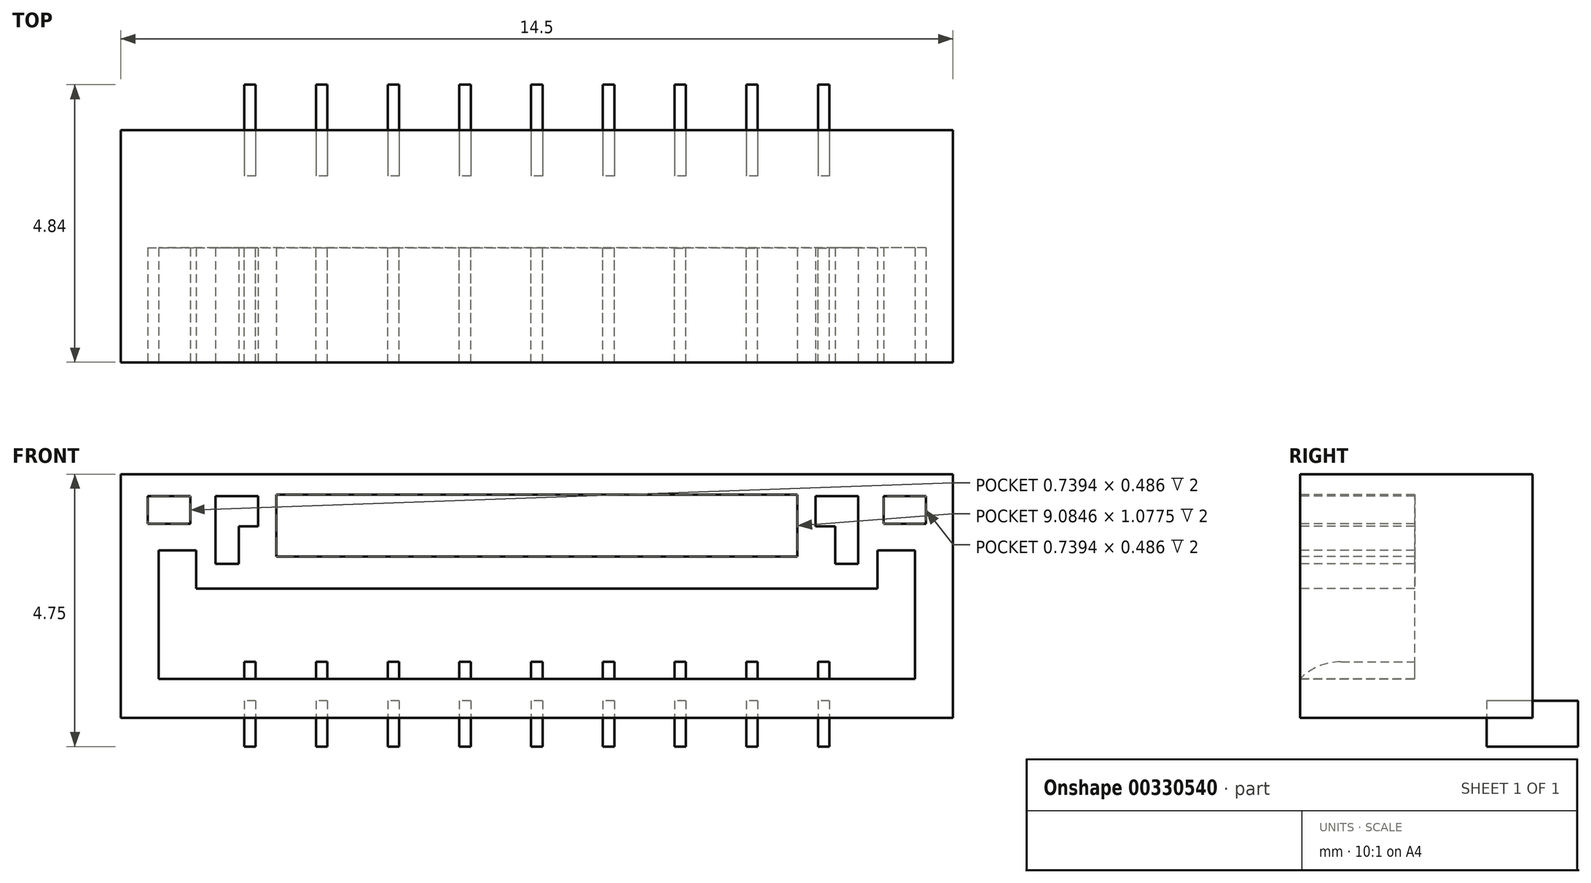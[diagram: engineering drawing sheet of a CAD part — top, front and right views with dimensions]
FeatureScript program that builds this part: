
annotation { "Feature Type Name" : "Feature", "Feature Type Description" : "" }
export const myFeature = defineFeature(function(context is Context, id is Id, definition is map)
    precondition{}
    {
        {
            var Q0;
            Q0=qCreatedBy(makeId("Top.planeOp"),FACE);
            var sketch = newSketch(context, id + "F0", { "sketchPlane" : qUnion([Q0])});
            skLineSegment(sketch, "E0.bottom", {"start": v(7.25, -2.02) * mm, "end": v(-7.25, -2.03) * mm});
            skLineSegment(sketch, "E0.top", {"start": v(7.25, 2.03) * mm, "end": v(-7.25, 2.02) * mm});
            skLineSegment(sketch, "E0.left", {"start": v(7.25, -2.02) * mm, "end": v(7.25, 2.03) * mm});
            skLineSegment(sketch, "E0.right", {"start": v(-7.25, -2.03) * mm, "end": v(-7.25, 2.02) * mm});
            skPoint(sketch, "E0.middle", {"position": v(0, 0) * mm});
            skSolve(sketch);
        }
        {
            var Q0;
            Q0 = qSketchRegion(id + "F0", true);
            extrude(context, id + "F1", {"entities" : qUnion([Q0]), "depth" : 4.25 * mm, "offsetDistance" : 25 * mm});
        }
        {
            var Q0;
            Q0=makeQuery(id+"F1.opExtrude","SWEPT_FACE",FACE,{"disambiguationData":[OSD([sQuery(id+"F0.wireOp",EDGE,"E0.bottom")])]});
            var sketch = newSketch(context, id + "F2", { "sketchPlane" : qUnion([Q0])});
            skLineSegment(sketch, "E1", {"start": v(0, 0.68) * mm, "end": v(-6.6, 0.68) * mm});
            skLineSegment(sketch, "E2", {"start": v(-6.6, 0.68) * mm, "end": v(-6.6, 2.92) * mm});
            skLineSegment(sketch, "E3", {"start": v(-6.6, 2.92) * mm, "end": v(-5.94, 2.92) * mm});
            skLineSegment(sketch, "E4", {"start": v(-5.94, 2.92) * mm, "end": v(-5.94, 2.25) * mm});
            skLineSegment(sketch, "E5", {"start": v(-5.94, 0.68) * mm, "end": v(0, 0.68) * mm});
            skLineSegment(sketch, "E6", {"start": v(0, 0.68) * mm, "end": v(0, 0.68) * mm});
            skLineSegment(sketch, "E7.bottom", {"start": v(-6.78, 3.87) * mm, "end": v(-6.04, 3.87) * mm});
            skLineSegment(sketch, "E7.top", {"start": v(-6.78, 3.38) * mm, "end": v(-6.04, 3.38) * mm});
            skLineSegment(sketch, "E7.left", {"start": v(-6.78, 3.87) * mm, "end": v(-6.78, 3.38) * mm});
            skLineSegment(sketch, "E7.right", {"start": v(-6.04, 3.87) * mm, "end": v(-6.04, 3.38) * mm});
            skLineSegment(sketch, "E8.bottom", {"start": v(-4.54, 3.89) * mm, "end": v(0, 3.89) * mm});
            skLineSegment(sketch, "E8.top", {"start": v(-4.54, 2.81) * mm, "end": v(0, 2.81) * mm});
            skLineSegment(sketch, "E8.left", {"start": v(-4.54, 3.89) * mm, "end": v(-4.54, 2.81) * mm});
            skLineSegment(sketch, "E9", {"start": v(-5.6, 3.87) * mm, "end": v(-5.6, 2.68) * mm});
            skLineSegment(sketch, "E10", {"start": v(-5.6, 2.68) * mm, "end": v(-5.2, 2.68) * mm});
            skLineSegment(sketch, "E11", {"start": v(-5.2, 2.68) * mm, "end": v(-5.2, 3.34) * mm});
            skLineSegment(sketch, "E12", {"start": v(-5.2, 3.34) * mm, "end": v(-4.86, 3.34) * mm});
            skLineSegment(sketch, "E13", {"start": v(-4.86, 3.34) * mm, "end": v(-4.86, 3.87) * mm});
            skLineSegment(sketch, "E14", {"start": v(-4.86, 3.87) * mm, "end": v(-5.6, 3.87) * mm});
            skLineSegment(sketch, "E15.MirrorCS", {"start": v(5.94, 2.92) * mm, "end": v(5.94, 2.25) * mm});
            skLineSegment(sketch, "E16.MirrorCS", {"start": v(6.78, 3.87) * mm, "end": v(6.78, 3.38) * mm});
            skLineSegment(sketch, "E17.MirrorCS", {"start": v(6.04, 3.87) * mm, "end": v(6.04, 3.38) * mm});
            skLineSegment(sketch, "E18.MirrorCS", {"start": v(5.2, 3.34) * mm, "end": v(4.86, 3.34) * mm});
            skLineSegment(sketch, "E19.MirrorCS", {"start": v(5.6, 2.68) * mm, "end": v(5.2, 2.68) * mm});
            skLineSegment(sketch, "E20.MirrorCS", {"start": v(4.86, 3.34) * mm, "end": v(4.86, 3.87) * mm});
            skLineSegment(sketch, "E21.MirrorCS", {"start": v(6.78, 3.87) * mm, "end": v(6.04, 3.87) * mm});
            skLineSegment(sketch, "E22.MirrorCS", {"start": v(6.78, 3.38) * mm, "end": v(6.04, 3.38) * mm});
            skLineSegment(sketch, "E23.MirrorCS", {"start": v(5.94, 0.68) * mm, "end": v(0, 0.68) * mm});
            skLineSegment(sketch, "E24.MirrorCS", {"start": v(6.6, 2.92) * mm, "end": v(5.94, 2.92) * mm});
            skLineSegment(sketch, "E25.MirrorCS", {"start": v(6.6, 0.68) * mm, "end": v(6.6, 2.92) * mm});
            skLineSegment(sketch, "E26.MirrorCS", {"start": v(0, 0.68) * mm, "end": v(6.6, 0.68) * mm});
            skLineSegment(sketch, "E27.MirrorCS", {"start": v(5.6, 3.87) * mm, "end": v(5.6, 2.68) * mm});
            skLineSegment(sketch, "E28.MirrorCS", {"start": v(4.54, 3.89) * mm, "end": v(4.54, 2.81) * mm});
            skLineSegment(sketch, "E29.MirrorCS", {"start": v(4.54, 3.89) * mm, "end": v(0, 3.89) * mm});
            skLineSegment(sketch, "E30.MirrorCS", {"start": v(4.54, 2.81) * mm, "end": v(0, 2.81) * mm});
            skLineSegment(sketch, "E31.MirrorCS", {"start": v(4.86, 3.87) * mm, "end": v(5.6, 3.87) * mm});
            skLineSegment(sketch, "E32.MirrorCS", {"start": v(5.2, 2.68) * mm, "end": v(5.2, 3.34) * mm});
            skLineSegment(sketch, "E33", {"start": v(-5.94, 2.25) * mm, "end": v(5.94, 2.25) * mm});
            skSolve(sketch);
        }
        {
            var Q0;
            Q0 = qSketchRegion(id + "F2", true);
            extrude(context, id + "F3", {"entities" : qUnion([Q0]), "operationType" : NewBodyOperationType.REMOVE, "oppositeDirection" : true, "depth" : 2 * mm, "offsetDistance" : 25 * mm});
        }
        {
            var Q0;
            Q0=makeQuery(id+"F3.boolean.opBoolean","COPY",FACE,{"derivedFrom":makeQuery(id+"F3.opExtrude","SWEPT_FACE",FACE,{"disambiguationData":[OSD([sQuery(id+"F2.wireOp",EDGE,"E1"),sQuery(id+"F2.wireOp",EDGE,"E5"),sQuery(id+"F2.wireOp",EDGE,"E26.MirrorCS")])]})});
            var sketch = newSketch(context, id + "F4", { "sketchPlane" : qUnion([Q0])});
            skLineSegment(sketch, "E34", {"start": v(0, -1.03) * mm, "end": v(0, -4.7) * mm, "construction": true});
            skPoint(sketch, "E34.endSnap0", {"position": v(0, -2.03) * mm});
            skLineSegment(sketch, "E35.bottom", {"start": v(-1.15, -2.03) * mm, "end": v(-1.35, -2.03) * mm});
            skLineSegment(sketch, "E35.top", {"start": v(-1.15, -0.03) * mm, "end": v(-1.35, -0.03) * mm});
            skLineSegment(sketch, "E35.left", {"start": v(-1.15, -2.03) * mm, "end": v(-1.15, -0.03) * mm});
            skLineSegment(sketch, "E35.right", {"start": v(-1.35, -2.03) * mm, "end": v(-1.35, -0.03) * mm});
            skPoint(sketch, "E35.middle", {"position": v(-1.25, -1.03) * mm});
            skPoint(sketch, "E36.1.0.0", {"position": v(-2.5, -1.03) * mm});
            skLineSegment(sketch, "E36.1.0.1", {"start": v(-2.6, -2.03) * mm, "end": v(-2.6, -0.03) * mm});
            skLineSegment(sketch, "E36.1.0.2", {"start": v(-2.4, -2.03) * mm, "end": v(-2.6, -2.03) * mm});
            skLineSegment(sketch, "E36.1.0.3", {"start": v(-2.4, -2.03) * mm, "end": v(-2.4, -0.03) * mm});
            skLineSegment(sketch, "E36.1.0.4", {"start": v(-2.4, -0.03) * mm, "end": v(-2.6, -0.03) * mm});
            skPoint(sketch, "E36.2.0.0", {"position": v(-3.75, -1.03) * mm});
            skLineSegment(sketch, "E36.2.0.1", {"start": v(-3.85, -2.03) * mm, "end": v(-3.85, -0.03) * mm});
            skLineSegment(sketch, "E36.2.0.2", {"start": v(-3.65, -2.03) * mm, "end": v(-3.85, -2.03) * mm});
            skLineSegment(sketch, "E36.2.0.3", {"start": v(-3.65, -2.03) * mm, "end": v(-3.65, -0.03) * mm});
            skLineSegment(sketch, "E36.2.0.4", {"start": v(-3.65, -0.03) * mm, "end": v(-3.85, -0.03) * mm});
            skPoint(sketch, "E36.3.0.0", {"position": v(-5, -1.03) * mm});
            skLineSegment(sketch, "E36.3.0.1", {"start": v(-5.1, -2.03) * mm, "end": v(-5.1, -0.03) * mm});
            skLineSegment(sketch, "E36.3.0.2", {"start": v(-4.9, -2.03) * mm, "end": v(-5.1, -2.03) * mm});
            skLineSegment(sketch, "E36.3.0.3", {"start": v(-4.9, -2.03) * mm, "end": v(-4.9, -0.03) * mm});
            skLineSegment(sketch, "E36.3.0.4", {"start": v(-4.9, -0.03) * mm, "end": v(-5.1, -0.03) * mm});
            skLineSegment(sketch, "E36.direction1", {"start": v(-1.35, -2.03) * mm, "end": v(-2.6, -2.03) * mm, "construction": true});
            skLineSegment(sketch, "E37.MirrorCS", {"start": v(4.9, -0.03) * mm, "end": v(5.1, -0.03) * mm});
            skLineSegment(sketch, "E38.MirrorCS", {"start": v(1.15, -2.03) * mm, "end": v(1.35, -2.03) * mm});
            skLineSegment(sketch, "E39.MirrorCS", {"start": v(3.65, -0.03) * mm, "end": v(3.85, -0.03) * mm});
            skLineSegment(sketch, "E40.MirrorCS", {"start": v(2.4, -2.03) * mm, "end": v(2.6, -2.03) * mm});
            skPoint(sketch, "E41.MirrorP", {"position": v(3.75, -1.03) * mm});
            skLineSegment(sketch, "E42.MirrorCS", {"start": v(5.1, -2.03) * mm, "end": v(5.1, -0.03) * mm});
            skPoint(sketch, "E43.MirrorP", {"position": v(1.25, -1.03) * mm});
            skLineSegment(sketch, "E44.MirrorCS", {"start": v(4.9, -2.03) * mm, "end": v(5.1, -2.03) * mm});
            skLineSegment(sketch, "E45.MirrorCS", {"start": v(4.9, -2.03) * mm, "end": v(4.9, -0.03) * mm});
            skLineSegment(sketch, "E46.MirrorCS", {"start": v(1.15, -0.03) * mm, "end": v(1.35, -0.03) * mm});
            skLineSegment(sketch, "E47.MirrorCS", {"start": v(1.15, -2.03) * mm, "end": v(1.15, -0.03) * mm});
            skLineSegment(sketch, "E48.MirrorCS", {"start": v(1.35, -2.03) * mm, "end": v(1.35, -0.03) * mm});
            skLineSegment(sketch, "E49.MirrorCS", {"start": v(2.6, -2.03) * mm, "end": v(2.6, -0.03) * mm});
            skLineSegment(sketch, "E50.MirrorCS", {"start": v(2.4, -2.03) * mm, "end": v(2.4, -0.03) * mm});
            skLineSegment(sketch, "E51.MirrorCS", {"start": v(2.4, -0.03) * mm, "end": v(2.6, -0.03) * mm});
            skLineSegment(sketch, "E52.MirrorCS", {"start": v(3.85, -2.03) * mm, "end": v(3.85, -0.03) * mm});
            skLineSegment(sketch, "E53.MirrorCS", {"start": v(3.65, -2.03) * mm, "end": v(3.65, -0.03) * mm});
            skLineSegment(sketch, "E54.MirrorCS", {"start": v(3.65, -2.03) * mm, "end": v(3.85, -2.03) * mm});
            skPoint(sketch, "E55.MirrorP", {"position": v(5, -1.03) * mm});
            skPoint(sketch, "E56.MirrorP", {"position": v(2.5, -1.03) * mm});
            skLineSegment(sketch, "E57.MirrorCS", {"start": v(1.35, -2.03) * mm, "end": v(2.6, -2.03) * mm, "construction": true});
            skLineSegment(sketch, "E58.bottom", {"start": v(0.1, -2.03) * mm, "end": v(-0.1, -2.03) * mm});
            skLineSegment(sketch, "E58.top", {"start": v(0.1, -0.03) * mm, "end": v(-0.1, -0.03) * mm});
            skLineSegment(sketch, "E58.left", {"start": v(0.1, -2.03) * mm, "end": v(0.1, -0.03) * mm});
            skLineSegment(sketch, "E58.right", {"start": v(-0.1, -2.03) * mm, "end": v(-0.1, -0.03) * mm});
            skPoint(sketch, "E58.middle", {"position": v(0, -1.03) * mm});
            skSolve(sketch);
        }
        {
            var Q0;
            Q0 = qSketchRegion(id + "F4", true);
            extrude(context, id + "F5", {"entities" : qUnion([Q0]), "depth" : .3 * mm, "offsetDistance" : 25 * mm});
        }
        {
            var Q0;
            Q0=makeQuery(id+"F5.opExtrude","CAP_EDGE",EDGE,{"disambiguationData":[OSD([sQuery(id+"F4.wireOp",EDGE,"E36.3.0.2")])],"isStart":false});
            var Q1;
            Q1=makeQuery(id+"F5.opExtrude","CAP_EDGE",EDGE,{"disambiguationData":[OSD([sQuery(id+"F4.wireOp",EDGE,"E36.2.0.2")])],"isStart":false});
            var Q2;
            Q2=makeQuery(id+"F5.opExtrude","CAP_EDGE",EDGE,{"disambiguationData":[OSD([sQuery(id+"F4.wireOp",EDGE,"E36.1.0.2")])],"isStart":false});
            var Q3;
            Q3=makeQuery(id+"F5.opExtrude","CAP_EDGE",EDGE,{"disambiguationData":[OSD([sQuery(id+"F4.wireOp",EDGE,"E35.bottom")])],"isStart":false});
            var Q4;
            Q4=makeQuery(id+"F5.opExtrude","CAP_EDGE",EDGE,{"disambiguationData":[OSD([sQuery(id+"F4.wireOp",EDGE,"E58.bottom")])],"isStart":false});
            var Q5;
            Q5=makeQuery(id+"F5.opExtrude","CAP_EDGE",EDGE,{"disambiguationData":[OSD([sQuery(id+"F4.wireOp",EDGE,"E38.MirrorCS")])],"isStart":false});
            var Q6;
            Q6=makeQuery(id+"F5.opExtrude","CAP_EDGE",EDGE,{"disambiguationData":[OSD([sQuery(id+"F4.wireOp",EDGE,"E40.MirrorCS")])],"isStart":false});
            var Q7;
            Q7=makeQuery(id+"F5.opExtrude","CAP_EDGE",EDGE,{"disambiguationData":[OSD([sQuery(id+"F4.wireOp",EDGE,"E54.MirrorCS")])],"isStart":false});
            var Q8;
            Q8=makeQuery(id+"F5.opExtrude","CAP_EDGE",EDGE,{"disambiguationData":[OSD([sQuery(id+"F4.wireOp",EDGE,"E44.MirrorCS")])],"isStart":false});
            fillet(context, id + "F6", {"entities" : qUnion([Q0, Q1, Q2, Q3, Q4, Q5, Q6, Q7, Q8]), "radius" : 1 * mm, "tangentPropagation" : true, "allowEdgeOverflow" : false});
        }
        {
            var Q0;
            Q0=makeQuery(id+"F1.opExtrude","CAP_FACE",FACE,{"disambiguationData":[OSD([sQuery(id+"F0.wireOp",EDGE,"E0.bottom"),sQuery(id+"F0.wireOp",EDGE,"E0.top"),sQuery(id+"F0.wireOp",EDGE,"E0.left"),sQuery(id+"F0.wireOp",EDGE,"E0.right")])],"isStart":true});
            var sketch = newSketch(context, id + "F7", { "sketchPlane" : qUnion([Q0])});
            skLineSegment(sketch, "E59.bottom", {"start": v(-4.9, -2.82) * mm, "end": v(-5.1, -2.82) * mm});
            skLineSegment(sketch, "E59.top", {"start": v(-4.9, -1.22) * mm, "end": v(-5.1, -1.22) * mm});
            skLineSegment(sketch, "E59.left", {"start": v(-4.9, -2.82) * mm, "end": v(-4.9, -1.22) * mm});
            skLineSegment(sketch, "E59.right", {"start": v(-5.1, -2.82) * mm, "end": v(-5.1, -1.22) * mm});
            skPoint(sketch, "E59.middle", {"position": v(-5, -2.02) * mm});
            skLineSegment(sketch, "E60", {"start": v(0, 0) * mm, "end": v(0, -3.72) * mm, "construction": true});
            skPoint(sketch, "E60.endSnap0", {"position": v(0, -2.03) * mm});
            skPoint(sketch, "E61.1.0.0", {"position": v(-3.75, -2.02) * mm});
            skLineSegment(sketch, "E61.1.0.1", {"start": v(-3.65, -2.82) * mm, "end": v(-3.65, -1.22) * mm});
            skLineSegment(sketch, "E61.1.0.2", {"start": v(-3.85, -2.82) * mm, "end": v(-3.85, -1.22) * mm});
            skLineSegment(sketch, "E61.1.0.3", {"start": v(-3.65, -2.82) * mm, "end": v(-3.85, -2.82) * mm});
            skLineSegment(sketch, "E61.1.0.4", {"start": v(-3.65, -1.22) * mm, "end": v(-3.85, -1.22) * mm});
            skPoint(sketch, "E61.2.0.0", {"position": v(-2.5, -2.02) * mm});
            skLineSegment(sketch, "E61.2.0.1", {"start": v(-2.4, -2.82) * mm, "end": v(-2.4, -1.22) * mm});
            skLineSegment(sketch, "E61.2.0.2", {"start": v(-2.6, -2.82) * mm, "end": v(-2.6, -1.22) * mm});
            skLineSegment(sketch, "E61.2.0.3", {"start": v(-2.4, -2.82) * mm, "end": v(-2.6, -2.82) * mm});
            skLineSegment(sketch, "E61.2.0.4", {"start": v(-2.4, -1.22) * mm, "end": v(-2.6, -1.22) * mm});
            skPoint(sketch, "E61.3.0.0", {"position": v(-1.25, -2.02) * mm});
            skLineSegment(sketch, "E61.3.0.1", {"start": v(-1.15, -2.82) * mm, "end": v(-1.15, -1.22) * mm});
            skLineSegment(sketch, "E61.3.0.2", {"start": v(-1.35, -2.82) * mm, "end": v(-1.35, -1.22) * mm});
            skLineSegment(sketch, "E61.3.0.3", {"start": v(-1.15, -2.82) * mm, "end": v(-1.35, -2.82) * mm});
            skLineSegment(sketch, "E61.3.0.4", {"start": v(-1.15, -1.22) * mm, "end": v(-1.35, -1.22) * mm});
            skPoint(sketch, "E61.4.0.0", {"position": v(0, -2.02) * mm});
            skLineSegment(sketch, "E61.4.0.1", {"start": v(0.1, -2.82) * mm, "end": v(0.1, -1.22) * mm});
            skLineSegment(sketch, "E61.4.0.2", {"start": v(-0.1, -2.82) * mm, "end": v(-0.1, -1.22) * mm});
            skLineSegment(sketch, "E61.4.0.3", {"start": v(0.1, -2.82) * mm, "end": v(-0.1, -2.82) * mm});
            skLineSegment(sketch, "E61.4.0.4", {"start": v(0.1, -1.22) * mm, "end": v(-0.1, -1.22) * mm});
            skPoint(sketch, "E61.5.0.0", {"position": v(1.25, -2.02) * mm});
            skLineSegment(sketch, "E61.5.0.1", {"start": v(1.35, -2.82) * mm, "end": v(1.35, -1.22) * mm});
            skLineSegment(sketch, "E61.5.0.2", {"start": v(1.15, -2.82) * mm, "end": v(1.15, -1.22) * mm});
            skLineSegment(sketch, "E61.5.0.3", {"start": v(1.35, -2.82) * mm, "end": v(1.15, -2.82) * mm});
            skLineSegment(sketch, "E61.5.0.4", {"start": v(1.35, -1.22) * mm, "end": v(1.15, -1.22) * mm});
            skPoint(sketch, "E61.6.0.0", {"position": v(2.5, -2.02) * mm});
            skLineSegment(sketch, "E61.6.0.1", {"start": v(2.6, -2.82) * mm, "end": v(2.6, -1.22) * mm});
            skLineSegment(sketch, "E61.6.0.2", {"start": v(2.4, -2.82) * mm, "end": v(2.4, -1.22) * mm});
            skLineSegment(sketch, "E61.6.0.3", {"start": v(2.6, -2.82) * mm, "end": v(2.4, -2.82) * mm});
            skLineSegment(sketch, "E61.6.0.4", {"start": v(2.6, -1.22) * mm, "end": v(2.4, -1.22) * mm});
            skPoint(sketch, "E61.7.0.0", {"position": v(3.75, -2.02) * mm});
            skLineSegment(sketch, "E61.7.0.1", {"start": v(3.85, -2.82) * mm, "end": v(3.85, -1.22) * mm});
            skLineSegment(sketch, "E61.7.0.2", {"start": v(3.65, -2.82) * mm, "end": v(3.65, -1.22) * mm});
            skLineSegment(sketch, "E61.7.0.3", {"start": v(3.85, -2.82) * mm, "end": v(3.65, -2.82) * mm});
            skLineSegment(sketch, "E61.7.0.4", {"start": v(3.85, -1.22) * mm, "end": v(3.65, -1.22) * mm});
            skPoint(sketch, "E61.8.0.0", {"position": v(5, -2.02) * mm});
            skLineSegment(sketch, "E61.8.0.1", {"start": v(5.1, -2.82) * mm, "end": v(5.1, -1.22) * mm});
            skLineSegment(sketch, "E61.8.0.2", {"start": v(4.9, -2.82) * mm, "end": v(4.9, -1.22) * mm});
            skLineSegment(sketch, "E61.8.0.3", {"start": v(5.1, -2.82) * mm, "end": v(4.9, -2.82) * mm});
            skLineSegment(sketch, "E61.8.0.4", {"start": v(5.1, -1.22) * mm, "end": v(4.9, -1.22) * mm});
            skLineSegment(sketch, "E61.direction1", {"start": v(-5.1, -2.82) * mm, "end": v(-3.85, -2.82) * mm, "construction": true});
            skSolve(sketch);
        }
        {
            var Q0;
            Q0 = qSketchRegion(id + "F7", true);
            extrude(context, id + "F8", {"entities" : qUnion([Q0]), "oppositeDirection" : true, "depth" : .3 * mm, "offsetDistance" : 25 * mm, "hasSecondDirection" : true, "secondDirectionOppositeDirection" : false, "secondDirectionDepth" : .5 * mm});
        }
    });
